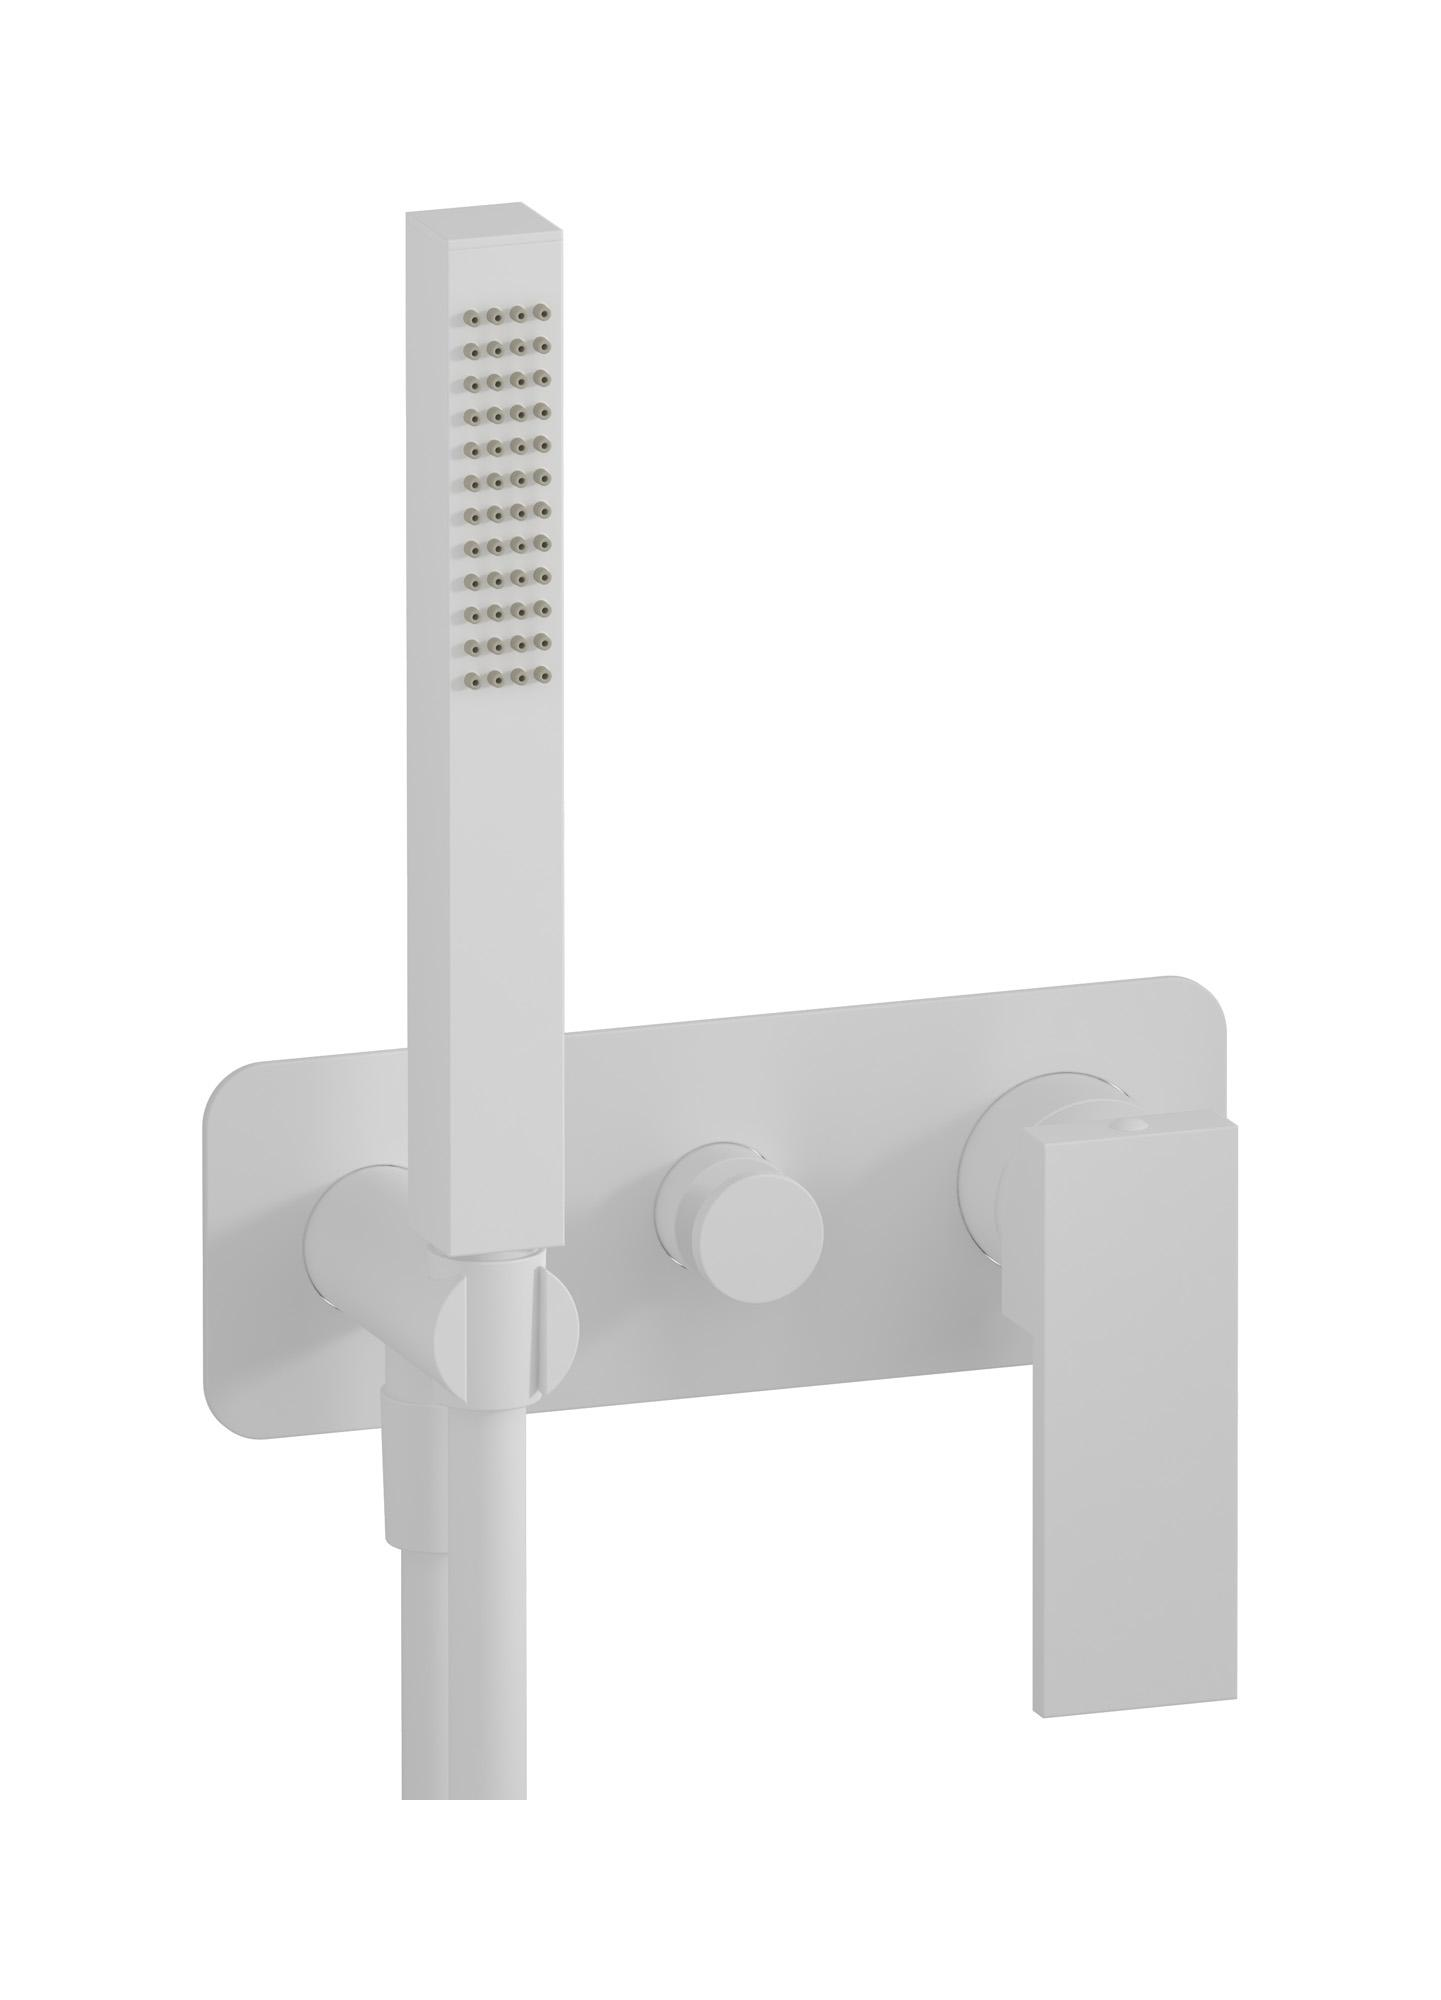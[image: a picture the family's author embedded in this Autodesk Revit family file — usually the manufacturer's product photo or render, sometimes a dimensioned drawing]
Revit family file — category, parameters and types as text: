
# Revit family: RU313
name_source: partatom
category: Apparecchi idraulici
units: mm (PartAtom-declared; Revit-internal decimal feet)

## family parameters
Basato su piano di lavoro = No
Condiviso = No
Mantieni orientamento annotazione = No
Numero OmniClass = 23.45.55.17
Punto di calcolo locali = No
Quota connettore circolare = Usa diametro
Sempre verticale = Sì
Taglio con vuoti quando caricato = No
Tipo di parte = Normale
Titolo OmniClass = Mixing Faucets

## types (12) — shared parameters
Cold water inlet = 10 mm  [stored 0.0328084 ft]
Commenti sul tipo = Exposed parts for manual wall mixer with two ways diverter and shower kit
Connessione CW = No
Connessione HW = No
Connessione di scarico = No
Connessione di ventilazione = No
Descrizione = Exposed parts for manual wall mixer with two ways diverter and shower kit
Hot water inlet = 10 mm  [stored 0.0328084 ft]
Produttore = IB Rubinetterie S.p.A.
URL = https://www.weareib.it
zero-valued in all types: Prospetto di default

## per-type parameters (varying)
| type | Finishes surface | Immagine tipo | Modello |
| Matt White | IB_matt white | RU313BO.jpg | RU313BO |
| Chrome | IB_Chrome | RU313CC.jpg | RU313CC |
| Black Chrome | IB_Black chrome | RU313CF.jpg | RU313CF |
| Brushed Black Chrome | IB_Brushed black chrome | RU313CS.jpg | RU313CS |
| Pale Gold | IB_Pale gold | RU313II.jpg | RU313II |
| Brushed Pale Gold | IB_brushed pale gold | RU313IS.jpg | RU313IS |
| Matt Black | IB_matt black | RU313NP.jpg | RU313NP |
| Gold | IB_gold | RU313OO.jpg | RU313OO |
| Brushed Gold | IB_brushed gold | RU313OS.jpg | RU313OS |
| Rose Gold | IB_Rose gold | RU313RS.jpg | RU313RS |
| Brushed Rose Gold | IB_Brushed rose gold | RU313SR.jpg | RU313SR |
| Brushed Nickel | IB_Brushed nickel | RU313SS.jpg | RU313SS |

note: [stored X ft] marks values corroborated as IEEE doubles in the binary element streams (Revit-internal decimal feet)
